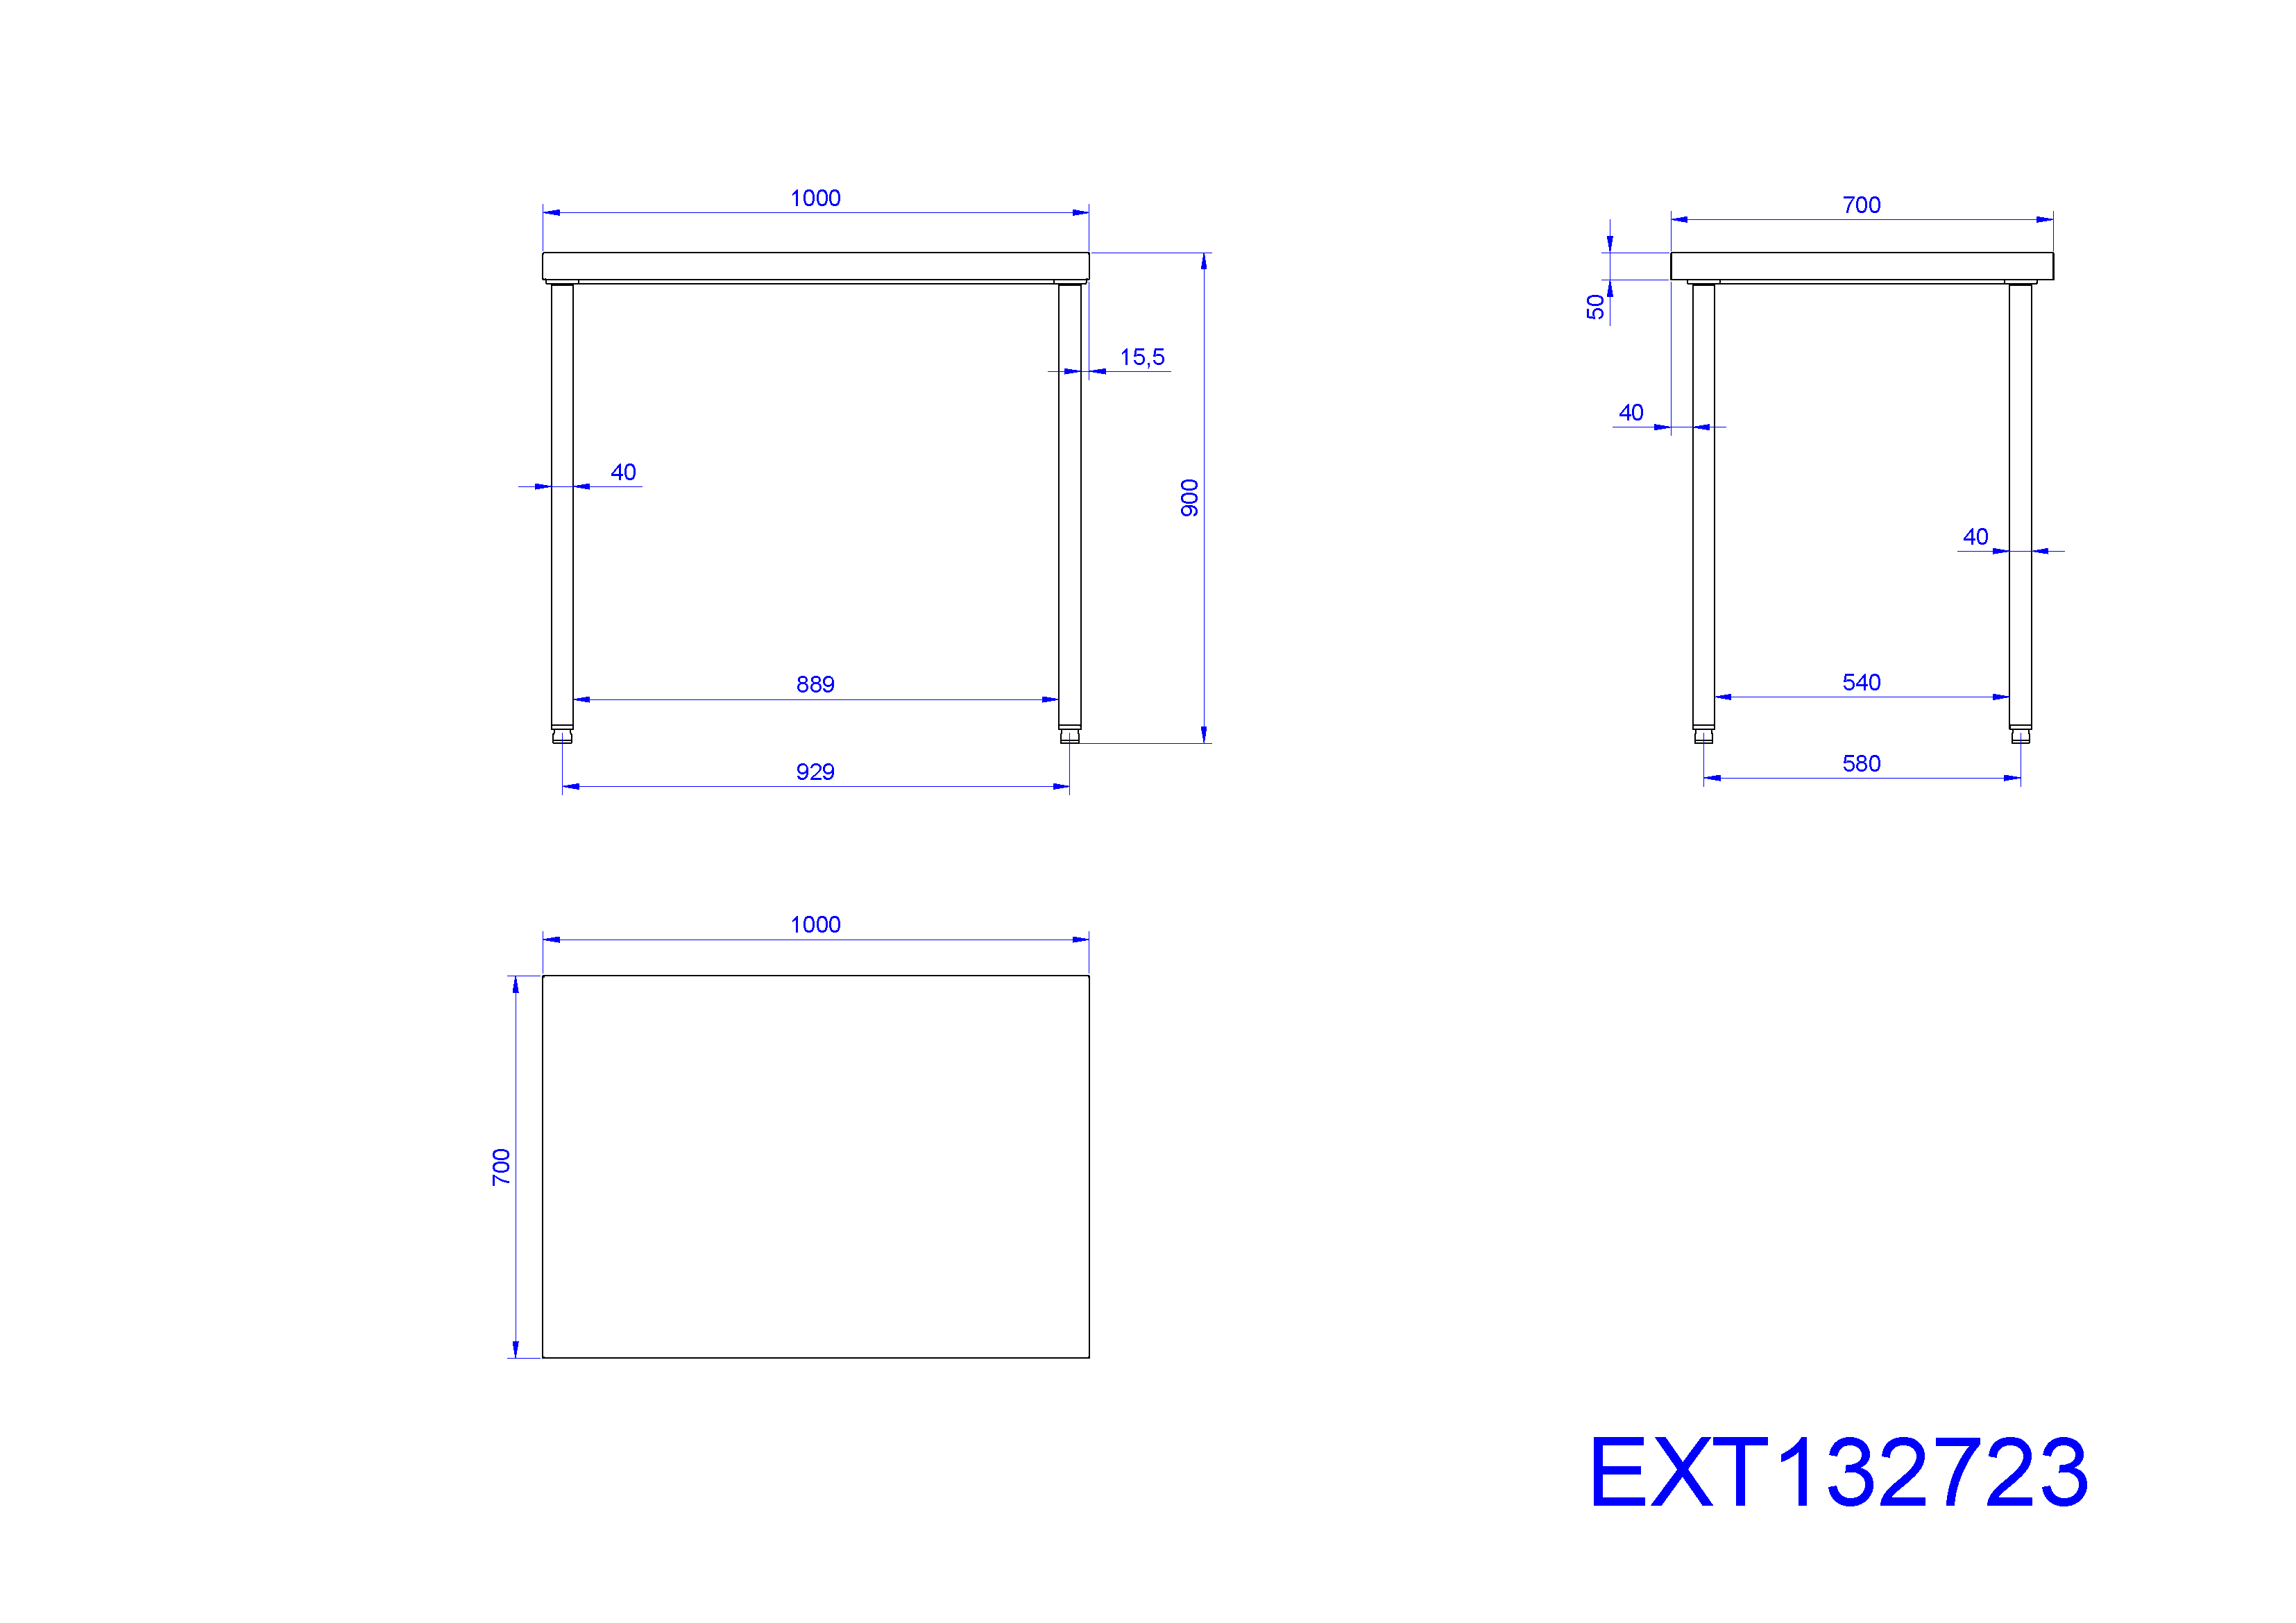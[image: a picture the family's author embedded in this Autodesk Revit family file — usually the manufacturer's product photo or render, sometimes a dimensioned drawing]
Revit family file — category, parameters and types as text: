
# Revit family: QF_ELECTROLUXPROFESSIONAL_133051_TG1600EN
name_source: partatom
category: Specialty Equipment
units: mm (PartAtom-declared; Revit-internal decimal feet)

## family parameters
Always vertical = Yes
Cut with Voids When Loaded = No
Part Type = Normal
Room Calculation Point = No
Round Connector Dimension = Use Diameter
Shared = No
Work Plane-Based = No

## types (1)
- Standard
    Accessory = No
    Cold Water Size = 0 mm
    Compressed Air Pressure = 0.0 Pa
    Compressed Air Size = 0 mm
    Compressed Air Volume = 0.0 L/s
    Condensate Return Size = 0 mm
    Cycle = 0 Hz
    Default Elevation = 0 mm  [stored 0 ft]
    Depth Actual = 700 mm  [stored 2.29659 ft]
    Description = WORK TABLE 1600 MM
    Direct Waste Size = 0 mm
    Gas Input Pressure = 0
    Gas KW = 0
    Gas Size = 0 mm
    HP = 0 HP
    Height Actual = 900 mm  [stored 2.95276 ft]
    Hot Water Size = 0 mm
    Item Number = 133051
    Length Actual = 1600 mm  [stored 5.24934 ft]
    Manufacturer = Electrolux Professional
    Model = TG1600EN
    Phase = 0
    Refrigerant Compressor Remote = Yes
    Refrigeration Liquid Line Size = 0 mm  [stored 0 ft]
    Refrigeration Suction Line Size = 0 mm  [stored 0 ft]
    Steam Consumption per Hour = 0
    Steam Supply Maximum Pressure = 0.0 Pa
    Steam Supply Minimum Pressure = 0.0 Pa
    Steam Supply Size = 0 mm
    URL = http://www.electroluxprofessional.com
    URL Manufacturer = http://www.electroluxprofessional.com
    Volts = 0 V
    Watts = 0 W
    Weight = 50.00 kg

note: source unit labels omitted for Gas Input Pressure — the stored unit's dimension contradicts the parameter name (converter mislabeling)

note: [stored X ft] marks values corroborated as IEEE doubles in the binary element streams (Revit-internal decimal feet)

## geometry (parser evidence)
native form markers: Sweep x3
no freeform markers — native parametric forms only
